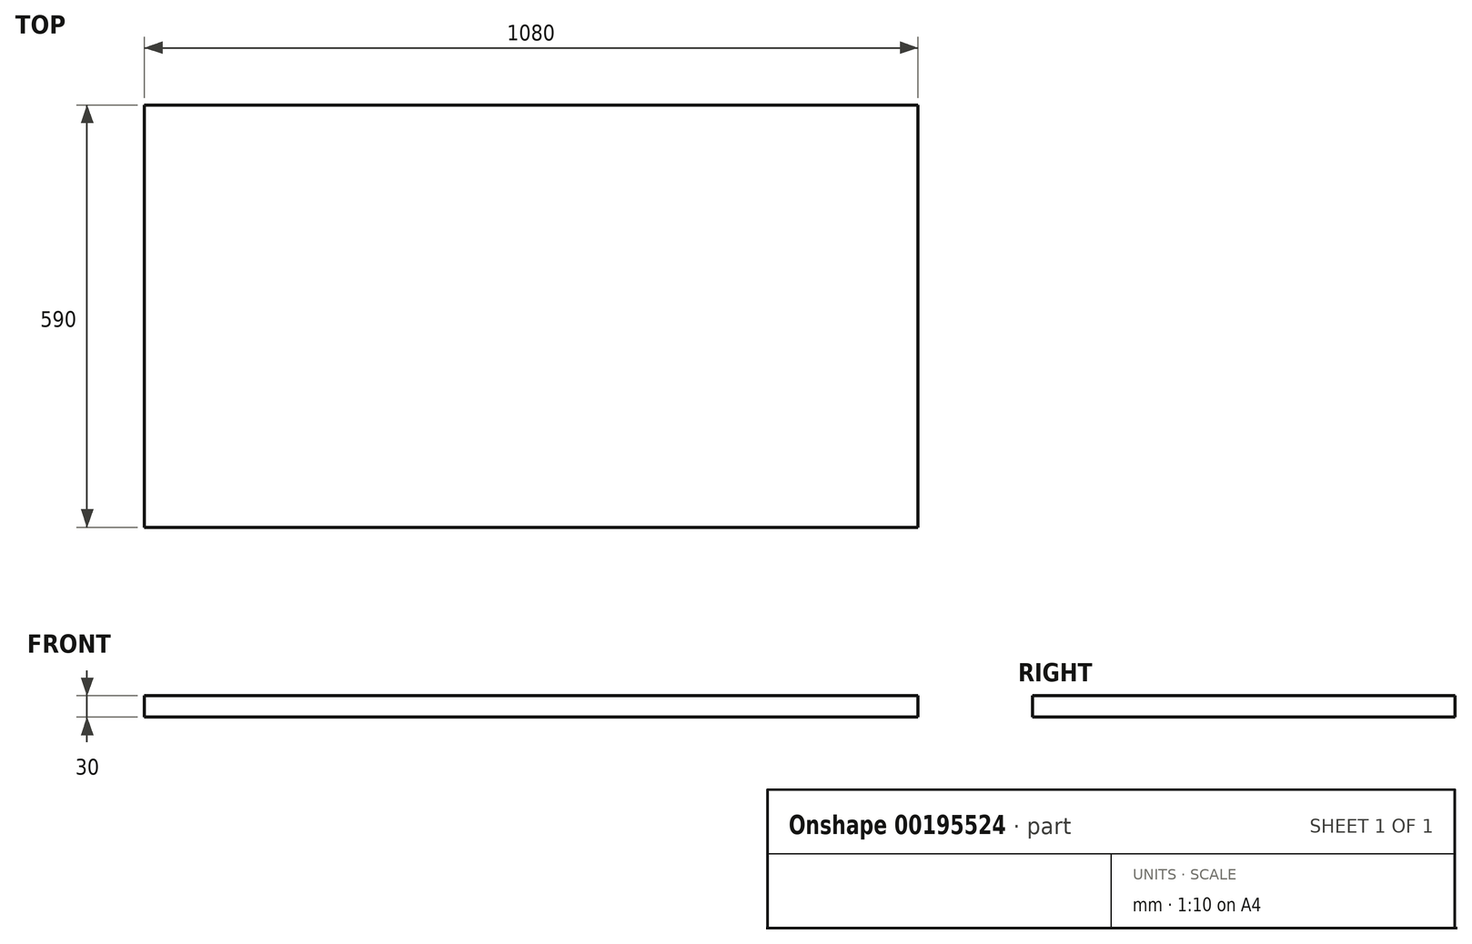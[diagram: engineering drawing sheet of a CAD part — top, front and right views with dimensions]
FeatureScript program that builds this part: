
annotation { "Feature Type Name" : "Feature", "Feature Type Description" : "" }
export const myFeature = defineFeature(function(context is Context, id is Id, definition is map)
    precondition{}
    {
        {
            var Q0;
            Q0=qCreatedBy(makeId("Top.planeOp"),FACE);
            var sketch = newSketch(context, id + "F0", { "sketchPlane" : qUnion([Q0])});
            skLineSegment(sketch, "E0.bottom", {"start": v(-603.57, -364.41) * mm, "end": v(476.43, -364.41) * mm});
            skLineSegment(sketch, "E0.top", {"start": v(-603.57, 225.59) * mm, "end": v(476.43, 225.59) * mm});
            skLineSegment(sketch, "E0.left", {"start": v(-603.57, -364.41) * mm, "end": v(-603.57, 225.59) * mm});
            skLineSegment(sketch, "E0.right", {"start": v(476.43, -364.41) * mm, "end": v(476.43, 225.59) * mm});
            skSolve(sketch);
        }
        {
            var Q0;
            Q0=makeQuery(id+"F0.imprint","IMPRINT",FACE,{"disambiguationData":[TD([[makeQuery(id+"F0.imprint","IMPRINT",EDGE,{"derivedFrom":sQuery(id+"F0.wireOp",EDGE,"E0.bottom")}),1.0]])]});
            extrude(context, id + "F1", {"entities" : qUnion([Q0]), "depth" : 30 * mm});
        }
    });
